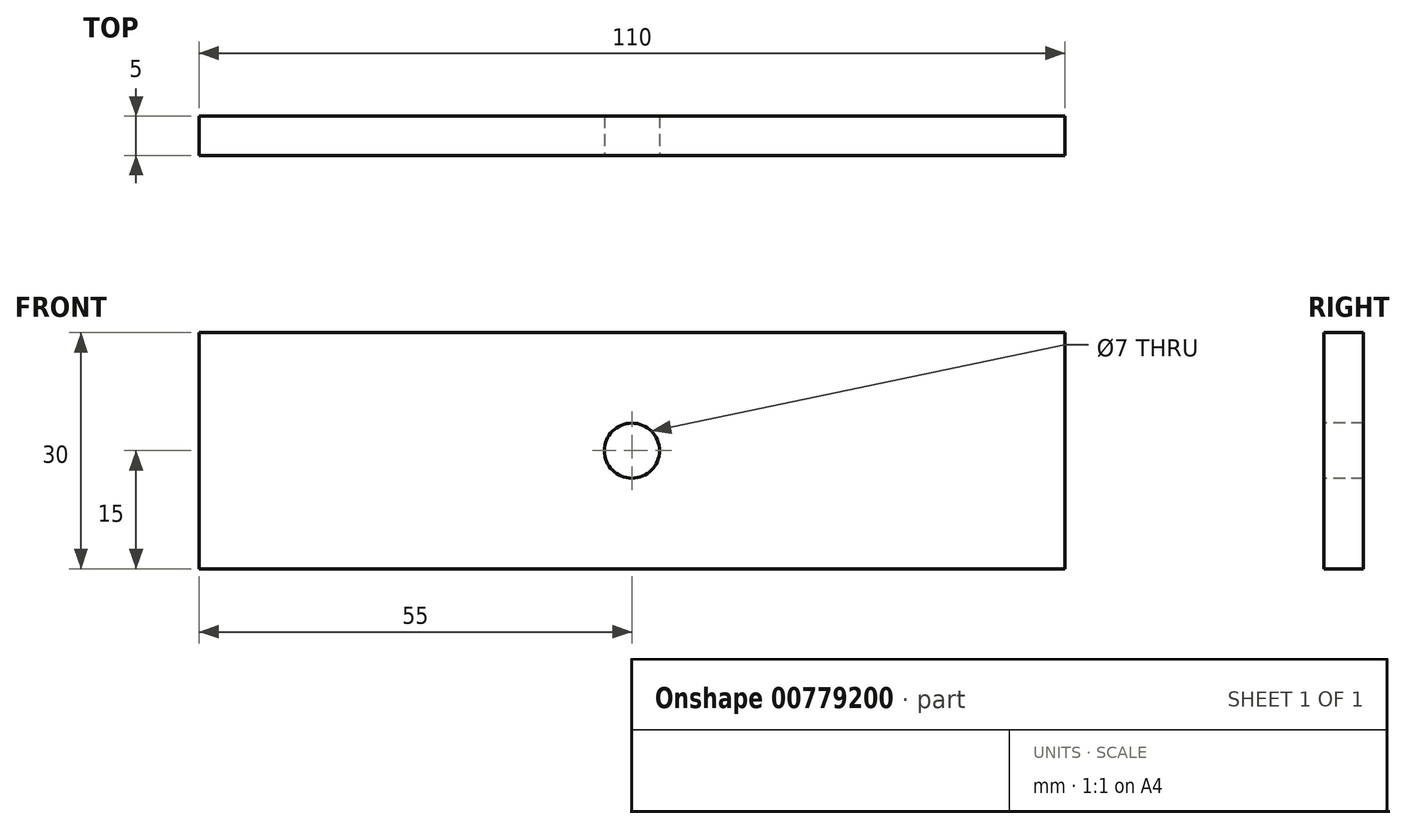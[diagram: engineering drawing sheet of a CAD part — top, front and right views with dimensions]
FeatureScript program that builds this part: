
annotation { "Feature Type Name" : "Feature", "Feature Type Description" : "" }
export const myFeature = defineFeature(function(context is Context, id is Id, definition is map)
    precondition{}
    {
        {
            var Q0;
            Q0=qCreatedBy(makeId("Front.planeOp"),FACE);
            var sketch = newSketch(context, id + "F0", { "sketchPlane" : qUnion([Q0])});
            skLineSegment(sketch, "E0.bottom", {"start": v(0, 0) * mm, "end": v(110, 0) * mm});
            skLineSegment(sketch, "E0.top", {"start": v(0, 30) * mm, "end": v(110, 30) * mm});
            skLineSegment(sketch, "E0.left", {"start": v(0, 0) * mm, "end": v(0, 30) * mm});
            skLineSegment(sketch, "E0.right", {"start": v(110, 0) * mm, "end": v(110, 30) * mm});
            skSolve(sketch);
        }
        {
            var Q0;
            Q0=makeQuery(id+"F0.imprint","IMPRINT",FACE,{"disambiguationData":[TD([[makeQuery(id+"F0.imprint","IMPRINT",EDGE,{"derivedFrom":sQuery(id+"F0.wireOp",EDGE,"E0.bottom")}),1.0]])]});
            extrude(context, id + "F1", {"entities" : qUnion([Q0]), "depth" : 5 * mm});
        }
        {
            var Q0;
            Q0=makeQuery(id+"F1.opExtrude","CAP_FACE",FACE,{"disambiguationData":[OSD([sQuery(id+"F0.wireOp",EDGE,"E0.bottom"),sQuery(id+"F0.wireOp",EDGE,"E0.top"),sQuery(id+"F0.wireOp",EDGE,"E0.left"),sQuery(id+"F0.wireOp",EDGE,"E0.right")])],"isStart":false});
            var sketch = newSketch(context, id + "F2", { "sketchPlane" : qUnion([Q0])});
            skCircle(sketch, "E1", {"center": v(55, 15) * mm, "radius": 3.5 * mm});
            skSolve(sketch);
        }
        {
            var Q0;
            Q0=qSketchRegion(id+"F2",true);
            extrude(context, id + "F3", {"entities" : qUnion([Q0]), "operationType" : NewBodyOperationType.REMOVE, "oppositeDirection" : true, "depth" : 25 * mm});
        }
    });
